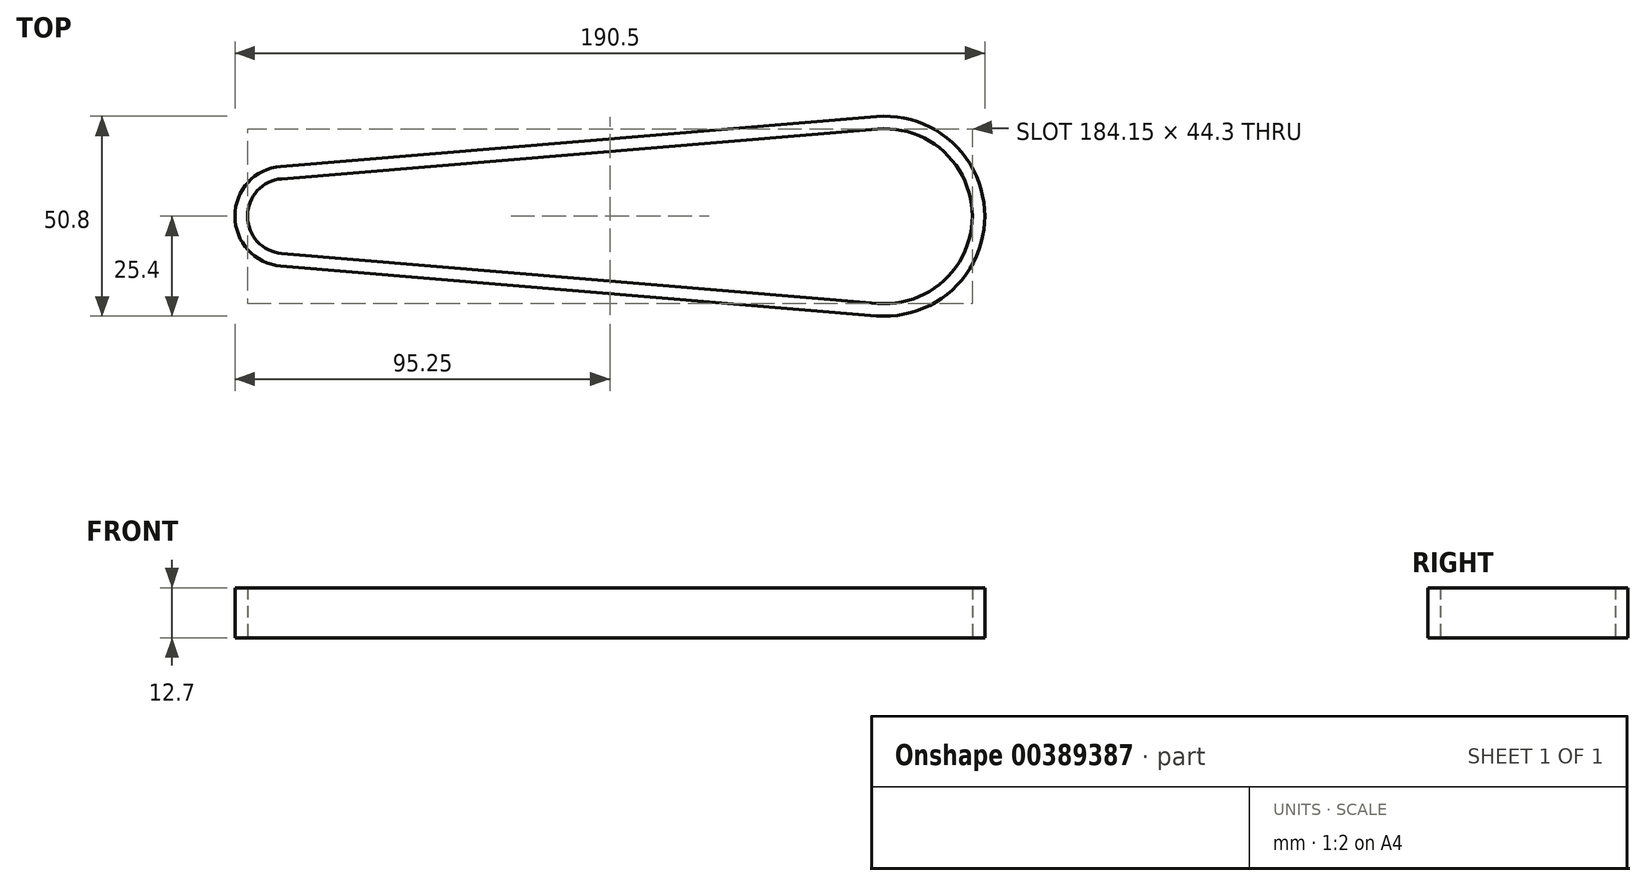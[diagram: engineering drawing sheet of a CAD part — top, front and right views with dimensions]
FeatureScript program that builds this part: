
annotation { "Feature Type Name" : "Feature", "Feature Type Description" : "" }
export const myFeature = defineFeature(function(context is Context, id is Id, definition is map)
    precondition{}
    {
        {
            var Q0;
            Q0=qCreatedBy(makeId("Top.planeOp"),FACE);
            var sketch = newSketch(context, id + "F0", { "sketchPlane" : qUnion([Q0])});
            skArc(sketch, "E0", {"start": v(-2.12, -25.31) * mm, "mid": v(25.4, 0) * mm, "end": v(-2.12, 25.31) * mm});
            skArc(sketch, "E1", {"start": v(-153.46, 12.66) * mm, "mid": v(-165.1, 0) * mm, "end": v(-153.46, -12.66) * mm});
            skLineSegment(sketch, "E2", {"start": v(-153.46, 12.66) * mm, "end": v(-2.12, 25.31) * mm});
            skLineSegment(sketch, "E3", {"start": v(-153.46, -12.66) * mm, "end": v(-2.12, -25.31) * mm});
            skArc(sketch, "E4", {"start": v(-153.2, 9.5) * mm, "mid": v(-161.93, 0) * mm, "end": v(-153.2, -9.5) * mm});
            skArc(sketch, "E5", {"start": v(-1.85, -22.15) * mm, "mid": v(22.22, 0) * mm, "end": v(-1.85, 22.15) * mm});
            skLineSegment(sketch, "E6", {"start": v(-153.2, 9.5) * mm, "end": v(-1.85, 22.15) * mm});
            skLineSegment(sketch, "E7", {"start": v(-153.2, -9.5) * mm, "end": v(-1.85, -22.15) * mm});
            skSolve(sketch);
        }
        {
            var Q0;
            Q0 = qSketchRegion(id + "F0", true);
            extrude(context, id + "F1", {"entities" : qUnion([Q0]), "depth" : 12.7 * mm});
        }
    });
